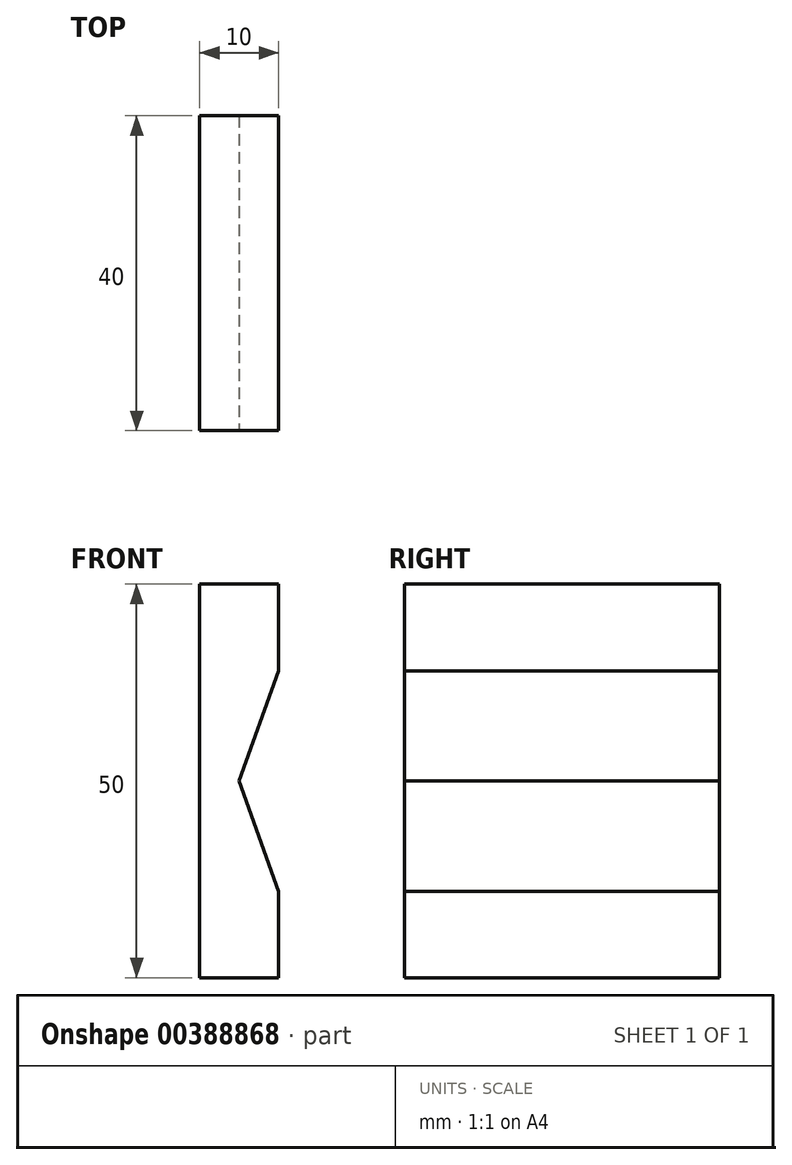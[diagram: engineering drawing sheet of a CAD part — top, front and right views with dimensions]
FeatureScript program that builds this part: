
annotation { "Feature Type Name" : "Feature", "Feature Type Description" : "" }
export const myFeature = defineFeature(function(context is Context, id is Id, definition is map)
    precondition{}
    {
        {
            var Q0;
            Q0=qCreatedBy(makeId("Top.planeOp"),FACE);
            var sketch = newSketch(context, id + "F0", { "sketchPlane" : qUnion([Q0])});
            skLineSegment(sketch, "E0.bottom", {"start": v(5, -20) * mm, "end": v(-5, -20) * mm});
            skLineSegment(sketch, "E0.top", {"start": v(5, 20) * mm, "end": v(-5, 20) * mm});
            skLineSegment(sketch, "E0.left", {"start": v(5, -20) * mm, "end": v(5, 20) * mm});
            skLineSegment(sketch, "E0.right", {"start": v(-5, -20) * mm, "end": v(-5, 20) * mm});
            skPoint(sketch, "E0.middle", {"position": v(0, 0) * mm});
            skSolve(sketch);
        }
        {
            var Q0;
            Q0 = qSketchRegion(id + "F0", true);
            extrude(context, id + "F1", {"entities" : qUnion([Q0]), "depth" : 50 * mm, "offsetDistance" : 25 * mm});
        }
        {
            var Q0;
            Q0=makeQuery(id+"F1.opExtrude","SWEPT_FACE",FACE,{"disambiguationData":[OSD([sQuery(id+"F0.wireOp",EDGE,"E0.bottom")])]});
            var sketch = newSketch(context, id + "F2", { "sketchPlane" : qUnion([Q0])});
            skLineSegment(sketch, "E1", {"start": v(-17.44, 25) * mm, "end": v(20.27, 25) * mm, "construction": true});
            skPoint(sketch, "E1.startSnap0", {"position": v(-5, 25) * mm});
            skLineSegment(sketch, "E2", {"start": v(0, -9.48) * mm, "end": v(0, 61.7) * mm, "construction": true});
            skPoint(sketch, "E2.endSnap0", {"position": v(0, 50) * mm});
            skLineSegment(sketch, "E3", {"start": v(5, 25) * mm, "end": v(5, 39) * mm});
            skLineSegment(sketch, "E4", {"start": v(5, 39) * mm, "end": v(0, 25) * mm});
            skPoint(sketch, "E4.endSnap0", {"position": v(1.41, 25) * mm});
            skLineSegment(sketch, "E5.MirrorCS", {"start": v(5, 11) * mm, "end": v(0, 25) * mm});
            skLineSegment(sketch, "E6.MirrorCS", {"start": v(5, 25) * mm, "end": v(5, 11) * mm});
            skSolve(sketch);
        }
        {
            var Q0;
            Q0 = qSketchRegion(id + "F2", true);
            extrude(context, id + "F3", {"entities" : qUnion([Q0]), "operationType" : NewBodyOperationType.REMOVE, "oppositeDirection" : true, "depth" : 43.6 * mm, "offsetDistance" : 25 * mm});
        }
    });
